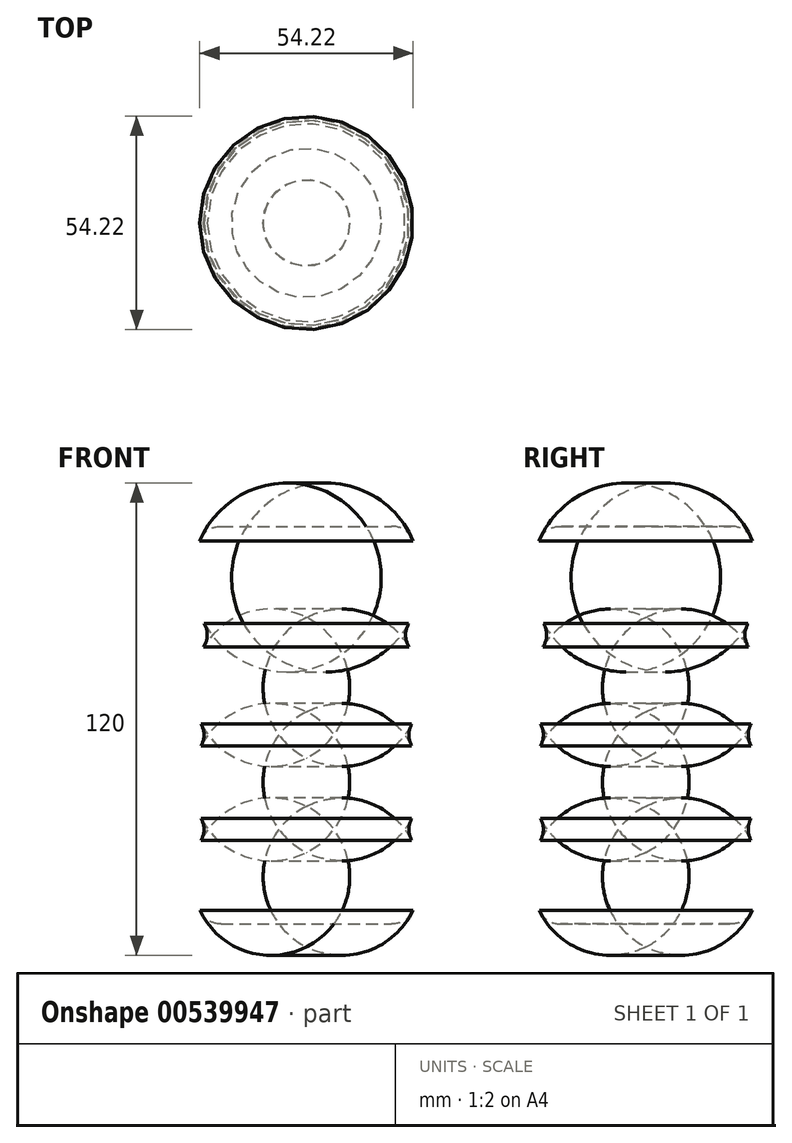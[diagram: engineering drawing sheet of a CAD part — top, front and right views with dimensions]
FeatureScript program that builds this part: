
annotation { "Feature Type Name" : "Feature", "Feature Type Description" : "" }
export const myFeature = defineFeature(function(context is Context, id is Id, definition is map)
    precondition{}
    {
        {
            var Q0;
            Q0=qCreatedBy(makeId("Front.planeOp"),FACE);
            var sketch = newSketch(context, id + "F0", { "sketchPlane" : qUnion([Q0])});
            skLineSegment(sketch, "E0", {"start": v(0, 0) * mm, "end": v(0, 101) * mm});
            skLineSegment(sketch, "E1.0", {"start": v(29, 0) * mm, "end": v(29, 101) * mm, "construction": true});
            skPoint(sketch, "E2", {"position": v(0, 12) * mm});
            skPoint(sketch, "E3", {"position": v(0, 36) * mm});
            skPoint(sketch, "E4", {"position": v(0, 60) * mm});
            skPoint(sketch, "E5", {"position": v(0, 88) * mm});
            skLineSegment(sketch, "E6", {"start": v(0, 12) * mm, "end": v(29, 12) * mm, "construction": true});
            skLineSegment(sketch, "E7", {"start": v(0, 36) * mm, "end": v(29, 36) * mm, "construction": true});
            skLineSegment(sketch, "E8", {"start": v(0, 60) * mm, "end": v(29, 60) * mm, "construction": true});
            skLineSegment(sketch, "E9", {"start": v(0, 88) * mm, "end": v(29, 88) * mm, "construction": true});
            skArc(sketch, "E10", {"start": v(25, 0) * mm, "mid": v(29, 12) * mm, "end": v(25, 24) * mm});
            skPoint(sketch, "E11.startSnap0", {"position": v(14.5, 36) * mm});
            skArc(sketch, "E12", {"start": v(25, 48) * mm, "mid": v(28.98, 60.83) * mm, "end": v(23.96, 73.28) * mm});
            skArc(sketch, "E13", {"start": v(23.96, 73.28) * mm, "mid": v(28.98, 86.95) * mm, "end": v(25.17, 101) * mm});
            skPoint(sketch, "E13.startSnap0", {"position": v(14.5, 88) * mm});
            skArc(sketch, "E14", {"start": v(25, 24) * mm, "mid": v(29, 36) * mm, "end": v(25, 48) * mm});
            skLineSegment(sketch, "E15", {"start": v(0, 0) * mm, "end": v(25, 0) * mm});
            skLineSegment(sketch, "E16", {"start": v(0, 101) * mm, "end": v(25.17, 101) * mm});
            skLineSegment(sketch, "E17", {"start": v(0, 0) * mm, "end": v(0, -16.12) * mm, "construction": true});
            skSolve(sketch);
        }
        {
            var Q0;
            Q0 = qSketchRegion(id + "F0", true);
            var Q1;
            Q1=sQuery(id+"F0.wireOp",EDGE,"E0");
            revolve(context, id + "F1", {"entities" : qUnion([Q0]), "axis" : qUnion([Q1]), "revolveType" : RevolveType.FULL});
        }
        {
            var Q0;
            Q0=makeQuery(id+"F1.opRevolve","SWEPT_EDGE",EDGE,{"disambiguationData":[OSD([sQuery(id+"F0.wireOp",EDGE,"E12"),sQuery(id+"F0.wireOp",EDGE,"E13")])]});
            var Q1;
            Q1=makeQuery(id+"F1.opRevolve","SWEPT_EDGE",EDGE,{"disambiguationData":[OSD([sQuery(id+"F0.wireOp",EDGE,"E12"),sQuery(id+"F0.wireOp",EDGE,"E14")])]});
            var Q2;
            Q2=makeQuery(id+"F1.opRevolve","SWEPT_EDGE",EDGE,{"disambiguationData":[OSD([sQuery(id+"F0.wireOp",EDGE,"E10"),sQuery(id+"F0.wireOp",EDGE,"E14")])]});
            var Q3;
            Q3=makeQuery(id+"F1.opRevolve","SWEPT_EDGE",EDGE,{"disambiguationData":[OSD([sQuery(id+"F0.wireOp",EDGE,"E10"),sQuery(id+"F0.wireOp",EDGE,"E15")])]});
            var Q4;
            Q4=makeQuery(id+"F1.opRevolve","SWEPT_EDGE",EDGE,{"disambiguationData":[OSD([sQuery(id+"F0.wireOp",EDGE,"E13"),sQuery(id+"F0.wireOp",EDGE,"E16")])]});
            fillet(context, id + "F2", {"entities" : qUnion([Q0, Q1, Q2, Q3, Q4]), "radius" : 6 * mm, "tangentPropagation" : true, "rho" : 0.5, "crossSection" : FilletCrossSection.CONIC, "allowEdgeOverflow" : false});
        }
    });
